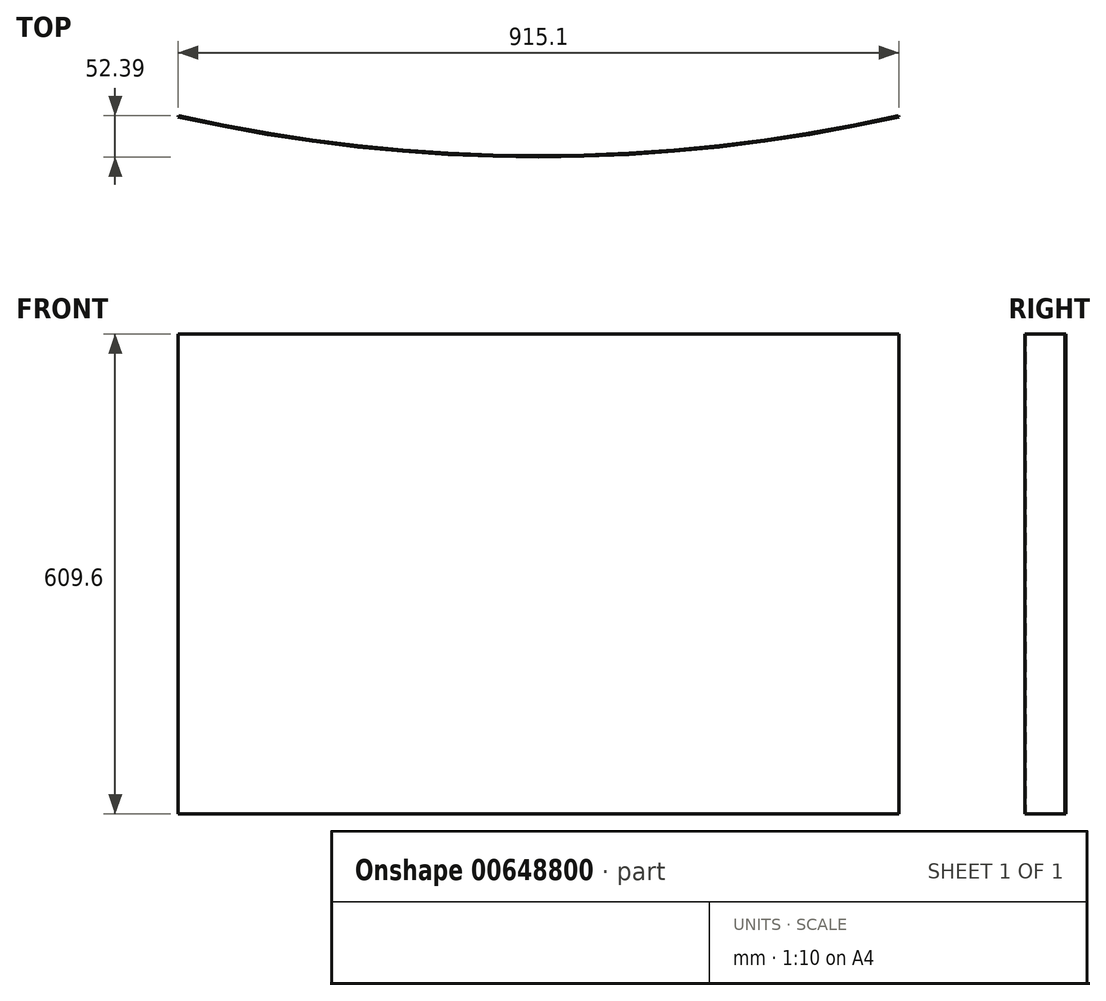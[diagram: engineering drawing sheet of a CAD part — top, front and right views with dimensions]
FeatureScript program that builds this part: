
annotation { "Feature Type Name" : "Feature", "Feature Type Description" : "" }
export const myFeature = defineFeature(function(context is Context, id is Id, definition is map)
    precondition{}
    {
        {
            var Q0;
            Q0=qCreatedBy(makeId("Top.planeOp"),FACE);
            var sketch = newSketch(context, id + "F0", { "sketchPlane" : qUnion([Q0])});
            skLineSegment(sketch, "E0", {"start": v(0, 0) * mm, "end": v(914.4, 0) * mm, "construction": true});
            skArc(sketch, "E1", {"start": v(0, 0) * mm, "mid": v(457.2, -50.8) * mm, "end": v(914.4, 0) * mm});
            skArc(sketch, "E2.0", {"start": v(-0.35, -1.55) * mm, "mid": v(457.2, -52.39) * mm, "end": v(914.75, -1.55) * mm});
            skLineSegment(sketch, "E3", {"start": v(0, 0) * mm, "end": v(-0.35, -1.55) * mm});
            skLineSegment(sketch, "E4", {"start": v(914.4, 0) * mm, "end": v(914.75, -1.55) * mm});
            skSolve(sketch);
        }
        {
            var Q0;
            Q0 = qSketchRegion(id + "F0", true);
            extrude(context, id + "F1", {"entities" : qUnion([Q0]), "depth" : 609.6 * mm, "offsetDistance" : 25.4 * mm});
        }
    });
